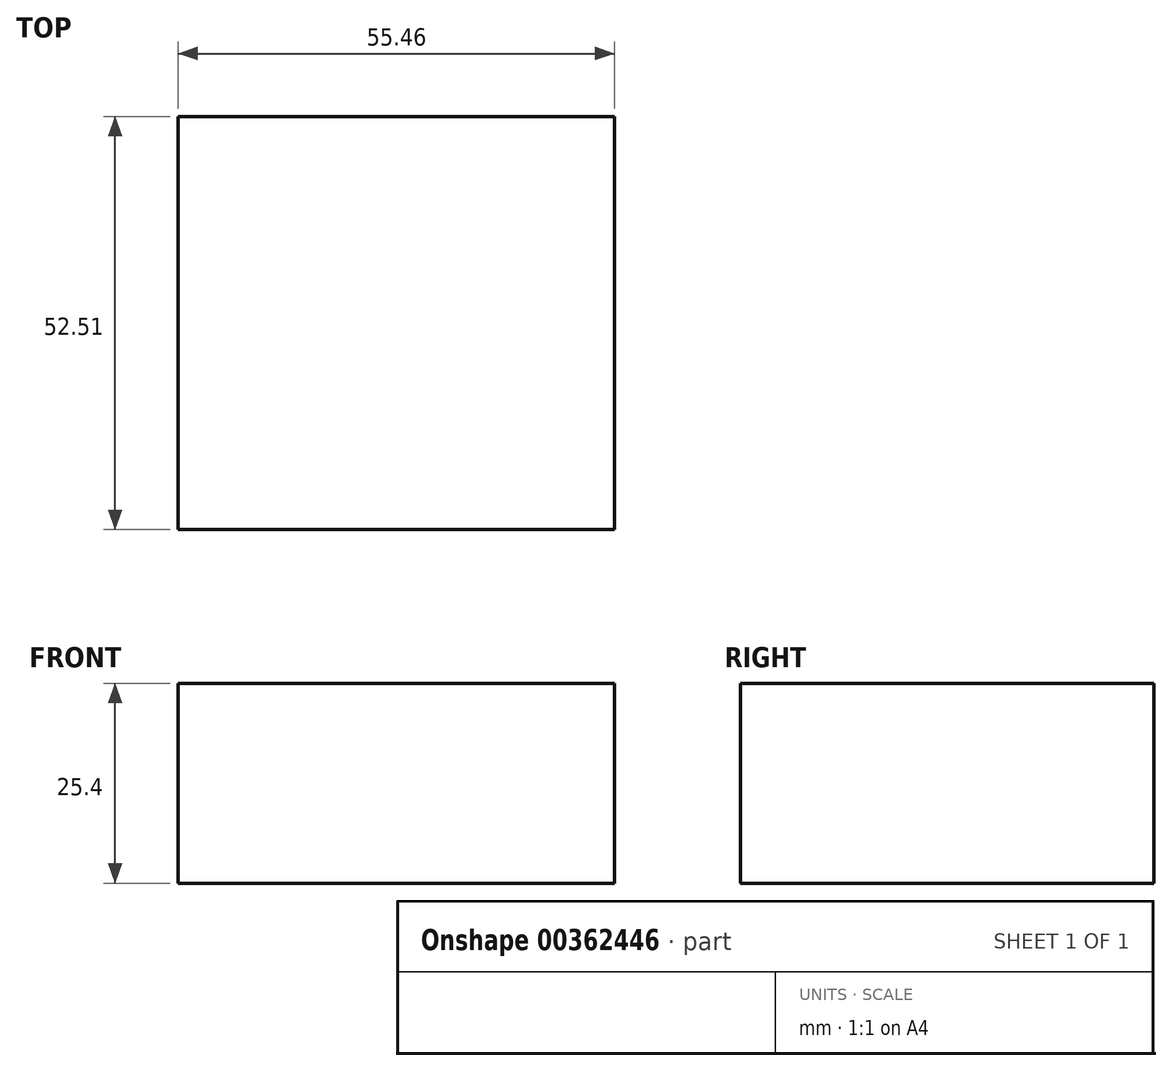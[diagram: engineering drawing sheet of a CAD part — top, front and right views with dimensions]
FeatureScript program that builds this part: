
annotation { "Feature Type Name" : "Feature", "Feature Type Description" : "" }
export const myFeature = defineFeature(function(context is Context, id is Id, definition is map)
    precondition{}
    {
        {
            var Q0;
            Q0=qCreatedBy(makeId("Top.planeOp"),FACE);
            var sketch = newSketch(context, id + "F0", { "sketchPlane" : qUnion([Q0])});
            skLineSegment(sketch, "E0.bottom", {"start": v(0, 0) * mm, "end": v(-55.46, 0) * mm});
            skLineSegment(sketch, "E0.top", {"start": v(0, 52.5) * mm, "end": v(-55.46, 52.5) * mm});
            skLineSegment(sketch, "E0.left", {"start": v(0, 0) * mm, "end": v(0, 52.5) * mm});
            skLineSegment(sketch, "E0.right", {"start": v(-55.46, 0) * mm, "end": v(-55.46, 52.5) * mm});
            skSolve(sketch);
        }
        {
            var Q0;
            Q0 = qSketchRegion(id + "F0", true);
            extrude(context, id + "F1", {"entities" : qUnion([Q0]), "depth" : 25.4 * mm});
        }
    });
